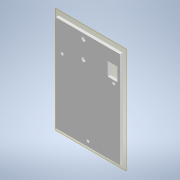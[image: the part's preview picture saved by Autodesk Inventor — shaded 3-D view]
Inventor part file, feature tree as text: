
AUTODESK INVENTOR PART (.ipt)
format: ipt  version: 2022 (Build 260153000, 153)  size: 161,280 bytes
history: native  units: mm
features: reference x14, other x6, extrude x4, sketch x4, projected_geometry x1
ambient origin geometry x8: Origin, YZ Plane, XZ Plane, XY Plane, X Axis, Y Axis, Z Axis, Center Point
bodies: Body1 (feature_tree)
feature tree (29):
  other  "Твердое тело1"
  other  "РабПлоскость1"
  extrude  "Выдавливание1"  Depth=4.0mm
  extrude  "Выдавливание2"  Depth=4.0mm
  extrude  "Выдавливание3"  Depth=4.0mm
  extrude  "Выдавливание4"  Depth=3.0mm TaperAngle=0.0deg
  sketch  "Эскиз1"
  reference  "Ссылка1"
  reference  "Ссылка2"
  reference  "Ссылка3"
  reference  "Ссылка4"
  reference  "Ссылка5"
  reference  "Ссылка6"
  reference  "Ссылка7"
  sketch  "Эскиз2"
  reference  "Ссылка8"
  reference  "Ссылка9"
  reference  "Ссылка10"
  reference  "Ссылка11"
  sketch  "Эскиз3"
  reference  "Ссылка12"
  reference  "Ссылка13"
  sketch  "Эскиз4"
  reference  "Ссылка14"
  projected_geometry  "Спроецированная петля1"
  other  "Сборка2"
  other  "корпус:1"
  other  "goruntu modulu:1"
  other  "Hold_18650-4:1"
